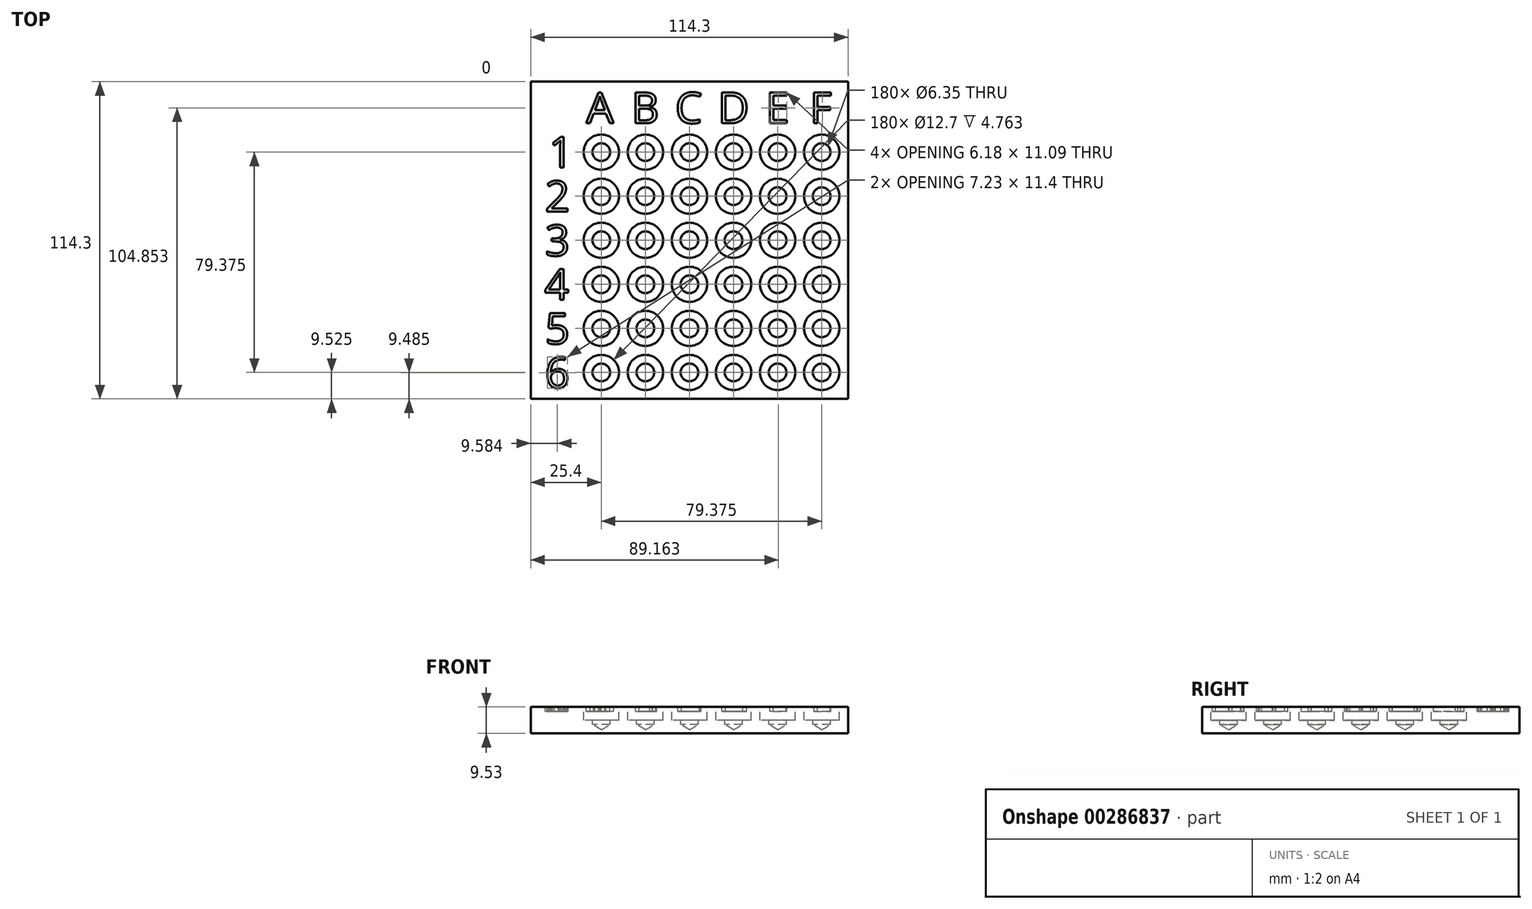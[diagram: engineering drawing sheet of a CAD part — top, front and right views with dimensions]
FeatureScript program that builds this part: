
annotation { "Feature Type Name" : "Feature", "Feature Type Description" : "" }
export const myFeature = defineFeature(function(context is Context, id is Id, definition is map)
    precondition{}
    {
        {
            var Q0;
            Q0=qCreatedBy(makeId("Top.planeOp"),FACE);
            var sketch = newSketch(context, id + "F0", { "sketchPlane" : qUnion([Q0])});
            skLineSegment(sketch, "E0.bottom", {"start": v(0, 114.3) * mm, "end": v(114.3, 114.3) * mm});
            skLineSegment(sketch, "E0.top", {"start": v(0, 0) * mm, "end": v(114.3, 0) * mm});
            skLineSegment(sketch, "E0.left", {"start": v(0, 114.3) * mm, "end": v(0, 0) * mm});
            skLineSegment(sketch, "E0.right", {"start": v(114.3, 114.3) * mm, "end": v(114.3, 0) * mm});
            skSolve(sketch);
        }
        {
            var Q0;
            Q0=makeQuery(id+"F0.imprint","IMPRINT",FACE,{"disambiguationData":[TD([[makeQuery(id+"F0.imprint","IMPRINT",EDGE,{"derivedFrom":sQuery(id+"F0.wireOp",EDGE,"E0.bottom")}),-1.0]])]});
            extrude(context, id + "F1", {"entities" : qUnion([Q0]), "depth" : 9.52 * mm});
        }
        {
            var Q0;
            Q0=makeQuery(id+"F1.opExtrude","CAP_FACE",FACE,{"disambiguationData":[OSD([sQuery(id+"F0.wireOp",EDGE,"E0.bottom"),sQuery(id+"F0.wireOp",EDGE,"E0.top"),sQuery(id+"F0.wireOp",EDGE,"E0.left"),sQuery(id+"F0.wireOp",EDGE,"E0.right")])],"isStart":false});
            var sketch = newSketch(context, id + "F2", { "sketchPlane" : qUnion([Q0])});
            skCircle(sketch, "E1", {"center": v(25.4, 88.9) * mm, "radius": 3.18 * mm});
            skCircle(sketch, "E2.0.1.0", {"center": v(25.4, 73.03) * mm, "radius": 3.18 * mm});
            skCircle(sketch, "E2.0.2.0", {"center": v(25.4, 57.15) * mm, "radius": 3.18 * mm});
            skCircle(sketch, "E2.0.3.0", {"center": v(25.4, 41.28) * mm, "radius": 3.18 * mm});
            skCircle(sketch, "E2.0.4.0", {"center": v(25.4, 25.4) * mm, "radius": 3.18 * mm});
            skCircle(sketch, "E2.0.5.0", {"center": v(25.4, 9.53) * mm, "radius": 3.18 * mm});
            skCircle(sketch, "E2.1.0.0", {"center": v(41.27, 88.9) * mm, "radius": 3.18 * mm});
            skCircle(sketch, "E2.1.1.0", {"center": v(41.27, 73.03) * mm, "radius": 3.18 * mm});
            skCircle(sketch, "E2.1.2.0", {"center": v(41.27, 57.15) * mm, "radius": 3.18 * mm});
            skCircle(sketch, "E2.1.3.0", {"center": v(41.27, 41.28) * mm, "radius": 3.18 * mm});
            skCircle(sketch, "E2.1.4.0", {"center": v(41.27, 25.4) * mm, "radius": 3.18 * mm});
            skCircle(sketch, "E2.1.5.0", {"center": v(41.27, 9.53) * mm, "radius": 3.18 * mm});
            skCircle(sketch, "E2.2.0.0", {"center": v(57.15, 88.9) * mm, "radius": 3.18 * mm});
            skCircle(sketch, "E2.2.1.0", {"center": v(57.15, 73.03) * mm, "radius": 3.18 * mm});
            skCircle(sketch, "E2.2.2.0", {"center": v(57.15, 57.15) * mm, "radius": 3.18 * mm});
            skCircle(sketch, "E2.2.3.0", {"center": v(57.15, 41.28) * mm, "radius": 3.18 * mm});
            skCircle(sketch, "E2.2.4.0", {"center": v(57.15, 25.4) * mm, "radius": 3.18 * mm});
            skCircle(sketch, "E2.2.5.0", {"center": v(57.15, 9.53) * mm, "radius": 3.18 * mm});
            skCircle(sketch, "E2.3.0.0", {"center": v(73.03, 88.9) * mm, "radius": 3.18 * mm});
            skCircle(sketch, "E2.3.1.0", {"center": v(73.03, 73.03) * mm, "radius": 3.18 * mm});
            skCircle(sketch, "E2.3.2.0", {"center": v(73.03, 57.15) * mm, "radius": 3.18 * mm});
            skCircle(sketch, "E2.3.3.0", {"center": v(73.03, 41.28) * mm, "radius": 3.18 * mm});
            skCircle(sketch, "E2.3.4.0", {"center": v(73.03, 25.4) * mm, "radius": 3.18 * mm});
            skCircle(sketch, "E2.3.5.0", {"center": v(73.03, 9.53) * mm, "radius": 3.18 * mm});
            skCircle(sketch, "E2.4.0.0", {"center": v(88.9, 88.9) * mm, "radius": 3.18 * mm});
            skCircle(sketch, "E2.4.1.0", {"center": v(88.9, 73.03) * mm, "radius": 3.18 * mm});
            skCircle(sketch, "E2.4.2.0", {"center": v(88.9, 57.15) * mm, "radius": 3.18 * mm});
            skCircle(sketch, "E2.4.3.0", {"center": v(88.9, 41.28) * mm, "radius": 3.18 * mm});
            skCircle(sketch, "E2.4.4.0", {"center": v(88.9, 25.4) * mm, "radius": 3.18 * mm});
            skCircle(sketch, "E2.4.5.0", {"center": v(88.9, 9.53) * mm, "radius": 3.18 * mm});
            skCircle(sketch, "E2.5.0.0", {"center": v(104.78, 88.9) * mm, "radius": 3.18 * mm});
            skCircle(sketch, "E2.5.1.0", {"center": v(104.78, 73.03) * mm, "radius": 3.18 * mm});
            skCircle(sketch, "E2.5.2.0", {"center": v(104.78, 57.15) * mm, "radius": 3.18 * mm});
            skCircle(sketch, "E2.5.3.0", {"center": v(104.78, 41.28) * mm, "radius": 3.18 * mm});
            skCircle(sketch, "E2.5.4.0", {"center": v(104.78, 25.4) * mm, "radius": 3.18 * mm});
            skCircle(sketch, "E2.5.5.0", {"center": v(104.78, 9.53) * mm, "radius": 3.18 * mm});
            skLineSegment(sketch, "E2.direction1", {"start": v(25.4, 88.9) * mm, "end": v(41.27, 88.9) * mm, "construction": true});
            skLineSegment(sketch, "E2.direction2", {"start": v(25.4, 88.9) * mm, "end": v(25.4, 73.03) * mm, "construction": true});
            skSolve(sketch);
        }
        {
            var Q0;
            Q0=sQuery(id+"F2.wireOp",VERTEX,"E1.center");
            var Q1;
            Q1=sQuery(id+"F2.wireOp",VERTEX,"E2.direction1.end");
            var Q2;
            Q2=sQuery(id+"F2.wireOp",VERTEX,"E2.2.0.0.center");
            var Q3;
            Q3=sQuery(id+"F2.wireOp",VERTEX,"E2.3.0.0.center");
            var Q4;
            Q4=sQuery(id+"F2.wireOp",VERTEX,"E2.4.0.0.center");
            var Q5;
            Q5=sQuery(id+"F2.wireOp",VERTEX,"E2.5.0.0.center");
            var Q6;
            Q6=sQuery(id+"F2.wireOp",VERTEX,"E2.5.1.0.center");
            var Q7;
            Q7=sQuery(id+"F2.wireOp",VERTEX,"E2.4.1.0.center");
            var Q8;
            Q8=sQuery(id+"F2.wireOp",VERTEX,"E2.3.1.0.center");
            var Q9;
            Q9=sQuery(id+"F2.wireOp",VERTEX,"E2.2.1.0.center");
            var Q10;
            Q10=sQuery(id+"F2.wireOp",VERTEX,"E2.1.1.0.center");
            var Q11;
            Q11=sQuery(id+"F2.wireOp",VERTEX,"E2.0.1.0.center");
            var Q12;
            Q12=sQuery(id+"F2.wireOp",VERTEX,"E2.0.2.0.center");
            var Q13;
            Q13=sQuery(id+"F2.wireOp",VERTEX,"E2.1.2.0.center");
            var Q14;
            Q14=sQuery(id+"F2.wireOp",VERTEX,"E2.2.2.0.center");
            var Q15;
            Q15=sQuery(id+"F2.wireOp",VERTEX,"E2.3.2.0.center");
            var Q16;
            Q16=sQuery(id+"F2.wireOp",VERTEX,"E2.4.2.0.center");
            var Q17;
            Q17=sQuery(id+"F2.wireOp",VERTEX,"E2.5.2.0.center");
            var Q18;
            Q18=sQuery(id+"F2.wireOp",VERTEX,"E2.5.3.0.center");
            var Q19;
            Q19=sQuery(id+"F2.wireOp",VERTEX,"E2.4.3.0.center");
            var Q20;
            Q20=sQuery(id+"F2.wireOp",VERTEX,"E2.3.3.0.center");
            var Q21;
            Q21=sQuery(id+"F2.wireOp",VERTEX,"E2.2.3.0.center");
            var Q22;
            Q22=sQuery(id+"F2.wireOp",VERTEX,"E2.1.3.0.center");
            var Q23;
            Q23=sQuery(id+"F2.wireOp",VERTEX,"E2.0.3.0.center");
            var Q24;
            Q24=sQuery(id+"F2.wireOp",VERTEX,"E2.0.4.0.center");
            var Q25;
            Q25=sQuery(id+"F2.wireOp",VERTEX,"E2.1.4.0.center");
            var Q26;
            Q26=sQuery(id+"F2.wireOp",VERTEX,"E2.2.4.0.center");
            var Q27;
            Q27=sQuery(id+"F2.wireOp",VERTEX,"E2.3.4.0.center");
            var Q28;
            Q28=sQuery(id+"F2.wireOp",VERTEX,"E2.4.4.0.center");
            var Q29;
            Q29=sQuery(id+"F2.wireOp",VERTEX,"E2.5.4.0.center");
            var Q30;
            Q30=sQuery(id+"F2.wireOp",VERTEX,"E2.4.5.0.center");
            var Q31;
            Q31=sQuery(id+"F2.wireOp",VERTEX,"E2.3.5.0.center");
            var Q32;
            Q32=sQuery(id+"F2.wireOp",VERTEX,"E2.2.5.0.center");
            var Q33;
            Q33=sQuery(id+"F2.wireOp",VERTEX,"E2.5.5.0.center");
            var Q34;
            Q34=sQuery(id+"F2.wireOp",VERTEX,"E2.1.5.0.center");
            var Q35;
            Q35=sQuery(id+"F2.wireOp",VERTEX,"E2.0.5.0.center");
            var Q36;
            Q36=makeQuery(id+"F1.opExtrude","SWEPT_BODY",BODY,{"disambiguationData":[OSD([sQuery(id+"F0.wireOp",EDGE,"E0.bottom"),sQuery(id+"F0.wireOp",EDGE,"E0.top"),sQuery(id+"F0.wireOp",EDGE,"E0.left"),sQuery(id+"F0.wireOp",EDGE,"E0.right")])]});
            hole(context, id + "F3", {"style" : HoleStyle.C_BORE, "endStyle" : HoleEndStyle.BLIND, "holeDiameter" : 6.35 * mm, "cBoreDiameter" : 12.7 * mm, "cBoreDepth" : 4.76 * mm, "holeDepth" : 6.35 * mm, "tappedDepth" : 12.7 * mm, "tapClearance" : 3, "startFromSketch" : true, "locations" : qUnion([Q0, Q1, Q2, Q3, Q4, Q5, Q6, Q7, Q8, Q9, Q10, Q11, Q12, Q13, Q14, Q15, Q16, Q17, Q18, Q19, Q20, Q21, Q22, Q23, Q24, Q25, Q26, Q27, Q28, Q29, Q30, Q31, Q32, Q33, Q34, Q35]), "scope" : qUnion([Q36])});
        }
        {
            var Q0;
            Q0=makeQuery(id+"F1.opExtrude","CAP_FACE",FACE,{"disambiguationData":[OSD([sQuery(id+"F0.wireOp",EDGE,"E0.bottom"),sQuery(id+"F0.wireOp",EDGE,"E0.top"),sQuery(id+"F0.wireOp",EDGE,"E0.left"),sQuery(id+"F0.wireOp",EDGE,"E0.right")])],"isStart":false});
            var sketch = newSketch(context, id + "F4", { "sketchPlane" : qUnion([Q0])});
            skText(sketch, "E3", { "text": "1", "fontName": "OpenSans-Regular.ttf"});
            skText(sketch, "E4", { "text": "2", "fontName": "OpenSans-Regular.ttf"});
            skText(sketch, "E5", { "text": "3", "fontName": "OpenSans-Regular.ttf"});
            skText(sketch, "E6", { "text": "4", "fontName": "OpenSans-Regular.ttf"});
            skText(sketch, "E7", { "text": "5", "fontName": "OpenSans-Regular.ttf"});
            skText(sketch, "E8", { "text": "6", "fontName": "OpenSans-Regular.ttf"});
            skPoint(sketch, "E9", {"position": v(6.43, 88.9) * mm});
            skPoint(sketch, "E10", {"position": v(5.12, 73.03) * mm});
            skPoint(sketch, "E11", {"position": v(5.16, 57.15) * mm});
            skPoint(sketch, "E12", {"position": v(4.86, 41.28) * mm});
            skPoint(sketch, "E13", {"position": v(5.15, 25.4) * mm});
            skPoint(sketch, "E14", {"position": v(5.08, 9.53) * mm});
            skText(sketch, "E15", { "text": "A", "fontName": "OpenSans-Regular.ttf"});
            skText(sketch, "E16", { "text": "B", "fontName": "OpenSans-Regular.ttf"});
            skText(sketch, "E17", { "text": "C", "fontName": "OpenSans-Regular.ttf"});
            skText(sketch, "E18", { "text": "D", "fontName": "OpenSans-Regular.ttf"});
            skText(sketch, "E19", { "text": "E", "fontName": "OpenSans-Regular.ttf"});
            skText(sketch, "E20", { "text": "F", "fontName": "OpenSans-Regular.ttf"});
            skPoint(sketch, "E21", {"position": v(19.99, 104.9) * mm});
            skPoint(sketch, "E22", {"position": v(36.17, 104.9) * mm});
            skPoint(sketch, "E23", {"position": v(51.98, 104.9) * mm});
            skPoint(sketch, "E24", {"position": v(67.34, 104.9) * mm});
            skPoint(sketch, "E25", {"position": v(84.55, 104.9) * mm});
            skPoint(sketch, "E26", {"position": v(100.42, 104.9) * mm});
            const initialGuessF4  = {"E3": [0.00643, 0.08331, 1, 0, 0.01118], "E4": [0.00512, 0.06744, 1, 0, 0.01118], "E5": [0.00516, 0.05156, 1, 0, 0.01118], "E6": [0.00486, 0.03569, 1, 0, 0.01118], "E7": [0.00515, 0.01981, 1, 0, 0.01118], "E8": [0.00508, 0.00394, 1, 0, 0.01118], "E15": [0.01999, 0.09931, 1, 0, 0.01118], "E16": [0.03617, 0.09931, 1, 0, 0.01118], "E17": [0.05198, 0.09931, 1, 0, 0.01118], "E18": [0.06734, 0.09931, 1, 0, 0.01118], "E19": [0.08455, 0.09931, 1, 0, 0.01118], "E20": [0.10042, 0.09931, 1, 0, 0.01118]};
            skSetInitialGuess(sketch, initialGuessF4);
            skSolve(sketch);
        }
        {
            var Q0;
            Q0 = qSketchRegion(id + "F4", true);
            extrude(context, id + "F5", {"entities" : qUnion([Q0]), "operationType" : NewBodyOperationType.REMOVE, "oppositeDirection" : true, "depth" : 1.59 * mm});
        }
    });
